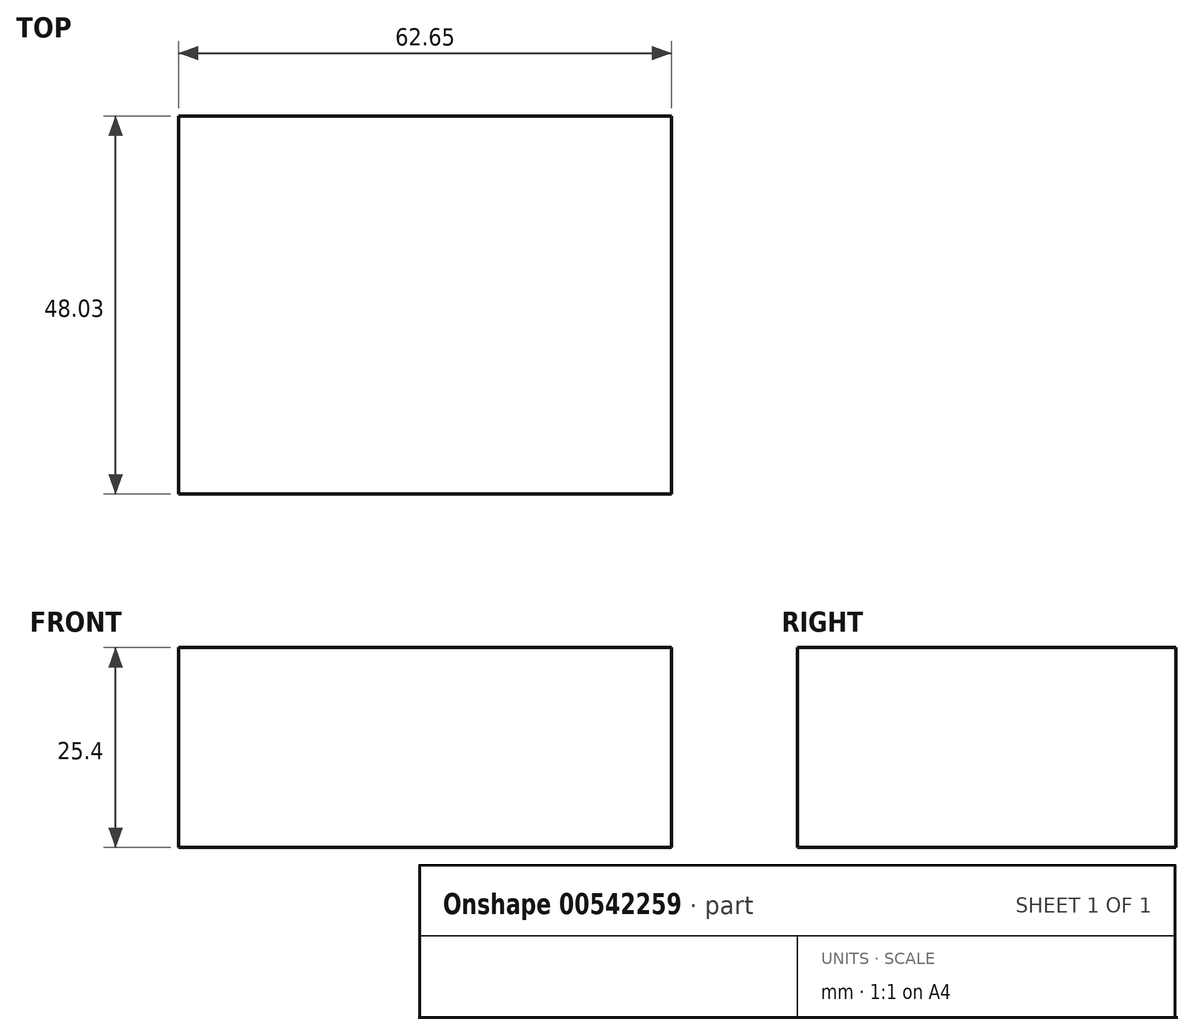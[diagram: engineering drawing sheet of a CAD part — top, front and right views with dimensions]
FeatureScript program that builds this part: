
annotation { "Feature Type Name" : "Feature", "Feature Type Description" : "" }
export const myFeature = defineFeature(function(context is Context, id is Id, definition is map)
    precondition{}
    {
        {
            var Q0;
            Q0=qCreatedBy(makeId("Top.planeOp"),FACE);
            var sketch = newSketch(context, id + "F0", { "sketchPlane" : qUnion([Q0])});
            skLineSegment(sketch, "E0.bottom", {"start": v(-62.65, -48.03) * mm, "end": v(0, -48.03) * mm});
            skLineSegment(sketch, "E0.top", {"start": v(-62.65, 0) * mm, "end": v(0, 0) * mm});
            skLineSegment(sketch, "E0.left", {"start": v(-62.65, -48.03) * mm, "end": v(-62.65, 0) * mm});
            skLineSegment(sketch, "E0.right", {"start": v(0, -48.03) * mm, "end": v(0, 0) * mm});
            skSolve(sketch);
        }
        {
            var Q0;
            Q0=sQuery(id+"F0.wireOp",EDGE,"E0.left");
            var Q1;
            Q1=sQuery(id+"F0.wireOp",EDGE,"E0.top");
            var Q2;
            Q2=sQuery(id+"F0.wireOp",EDGE,"E0.bottom");
            var Q3;
            Q3=sQuery(id+"F0.wireOp",EDGE,"E0.right");
            extrude(context, id + "F1", {"bodyType" : ToolBodyType.SURFACE, "surfaceEntities" : qUnion([Q0, Q1, Q2, Q3]), "depth" : 25.4 * mm, "offsetDistance" : 25.4 * mm});
        }
    });
